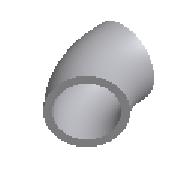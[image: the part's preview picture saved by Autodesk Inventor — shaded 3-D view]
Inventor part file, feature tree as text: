
AUTODESK INVENTOR PART (.ipt)
format: ipt  version: 2023.2 (Build 272271030, 271C)  size: 179,200 bytes
history: native  units: mm (DEFAULTED — no unit token found)
features: other x4, sketch x2, sweep x1
ambient origin geometry x8: Origin, YZ Plane, XZ Plane, XY Plane, X Axis, Y Axis, Z Axis, Center Point
bodies: Solid1 (feature_tree)
feature tree (7):
  sweep  "Sweep1"
  other  "Work Point1"
  other  "Work Point2"
  other  "Work Axis1"
  other  "Work Axis2"
  sketch  "Sketch1"  dims[d0=390.6mm d1=406.4mm]
  sketch  "Sketch2"  dims[d2=168.3mm d3=45.0deg d4=168.3mm d5=0.0mm d6=0.0mm]
